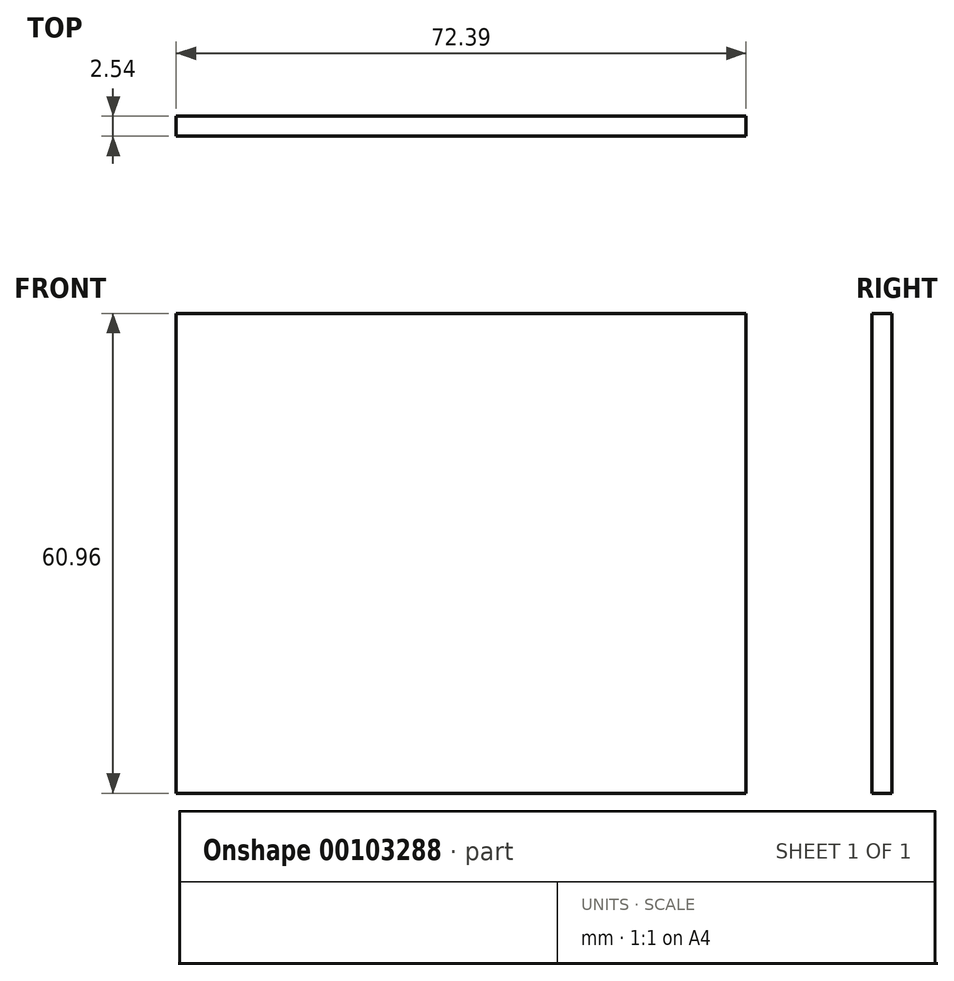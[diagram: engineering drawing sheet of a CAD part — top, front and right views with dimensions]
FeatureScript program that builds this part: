
annotation { "Feature Type Name" : "Feature", "Feature Type Description" : "" }
export const myFeature = defineFeature(function(context is Context, id is Id, definition is map)
    precondition{}
    {
        {
            var Q0;
            Q0=qCreatedBy(makeId("Front.planeOp"),FACE);
            var sketch = newSketch(context, id + "F0", { "sketchPlane" : qUnion([Q0])});
            skLineSegment(sketch, "E0.bottom", {"start": v(0, 0) * mm, "end": v(72.4, 0) * mm});
            skLineSegment(sketch, "E0.top", {"start": v(0, 60.96) * mm, "end": v(72.39, 60.96) * mm});
            skLineSegment(sketch, "E0.left", {"start": v(0, 0) * mm, "end": v(0, 60.96) * mm});
            skLineSegment(sketch, "E0.right", {"start": v(72.4, 0) * mm, "end": v(72.39, 60.96) * mm});
            skSolve(sketch);
        }
        {
            var Q0;
            Q0=makeQuery(id+"F0.imprint","IMPRINT",FACE,{"disambiguationData":[TD([[makeQuery(id+"F0.imprint","IMPRINT",EDGE,{"derivedFrom":sQuery(id+"F0.wireOp",EDGE,"E0.bottom")}),1.0]])]});
            extrude(context, id + "F1", {"entities" : qUnion([Q0]), "depth" : 2.54 * mm});
        }
    });
